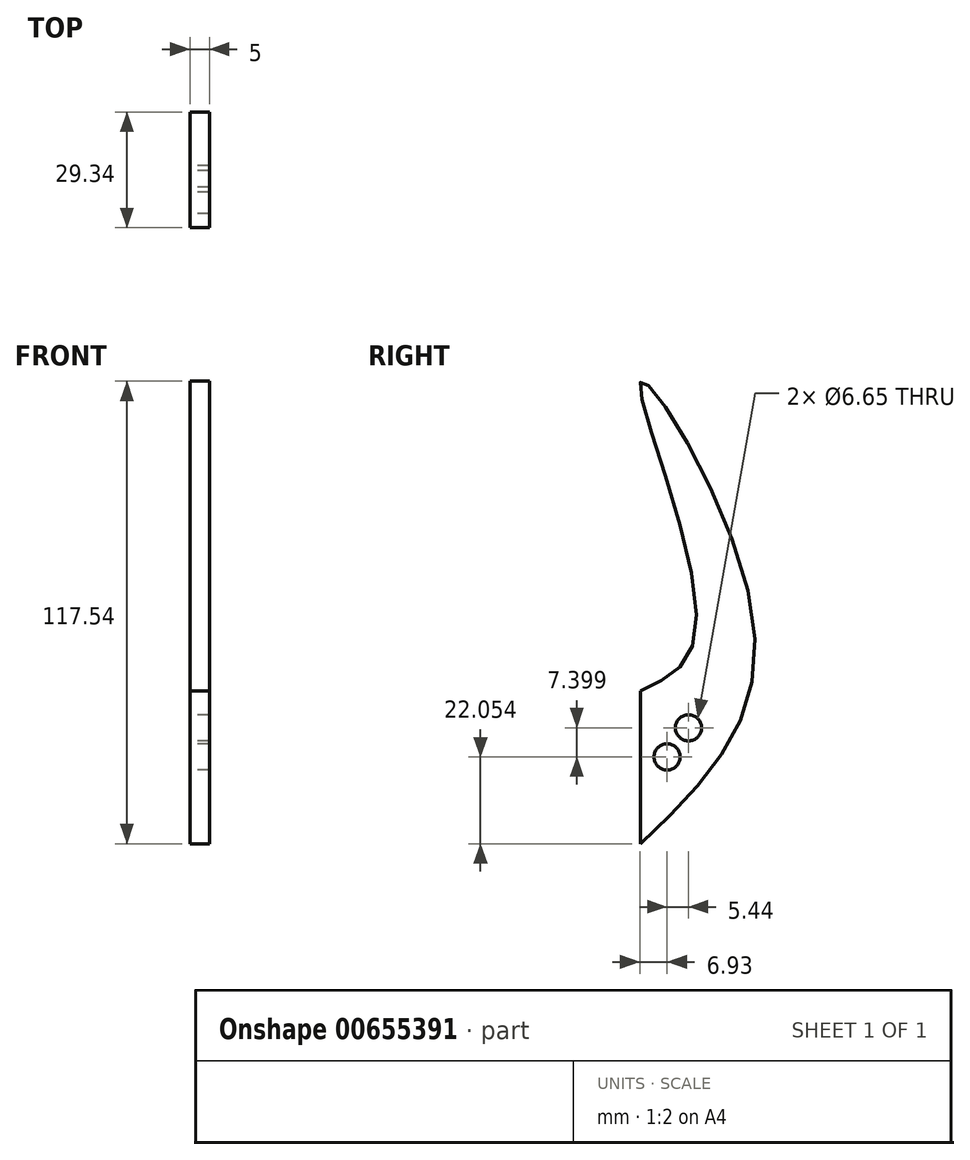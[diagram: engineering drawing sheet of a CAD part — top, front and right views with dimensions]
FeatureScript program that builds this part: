
annotation { "Feature Type Name" : "Feature", "Feature Type Description" : "" }
export const myFeature = defineFeature(function(context is Context, id is Id, definition is map)
    precondition{}
    {
        {
            var Q0;
            Q0=qCreatedBy(makeId("Right.planeOp"),FACE);
            var sketch = newSketch(context, id + "F0", { "sketchPlane" : qUnion([Q0])});
            skFitSpline(sketch, "E0", {"points": [v(0, -55.9) * mm, v(28.79, 0) * mm, v(0, 61.5) * mm, v(14.2, 0) * mm, v(0, -17.01) * mm], "startDerivative": vector(173.04, 165.43) * mm, "endDerivative": vector(-125.95, -56.55) * mm});
            skLineSegment(sketch, "E1", {"start": v(0, -17.01) * mm, "end": v(0, -55.9) * mm});
            skCircle(sketch, "E2", {"center": v(6.73, -33.84) * mm, "radius": 3.33 * mm});
            skCircle(sketch, "E3", {"center": v(12.17, -26.44) * mm, "radius": 3.33 * mm});
            skSolve(sketch);
        }
        {
            var Q0;
            Q0=makeQuery(id+"F0.imprint","IMPRINT",FACE,{"disambiguationData":[TD([[makeQuery(id+"F0.imprint","IMPRINT",EDGE,{"derivedFrom":sQuery(id+"F0.wireOp",EDGE,"E0")}),1.0]])]});
            extrude(context, id + "F1", {"entities" : qUnion([Q0]), "depth" : 5 * mm, "offsetDistance" : 25.4 * mm});
        }
    });
